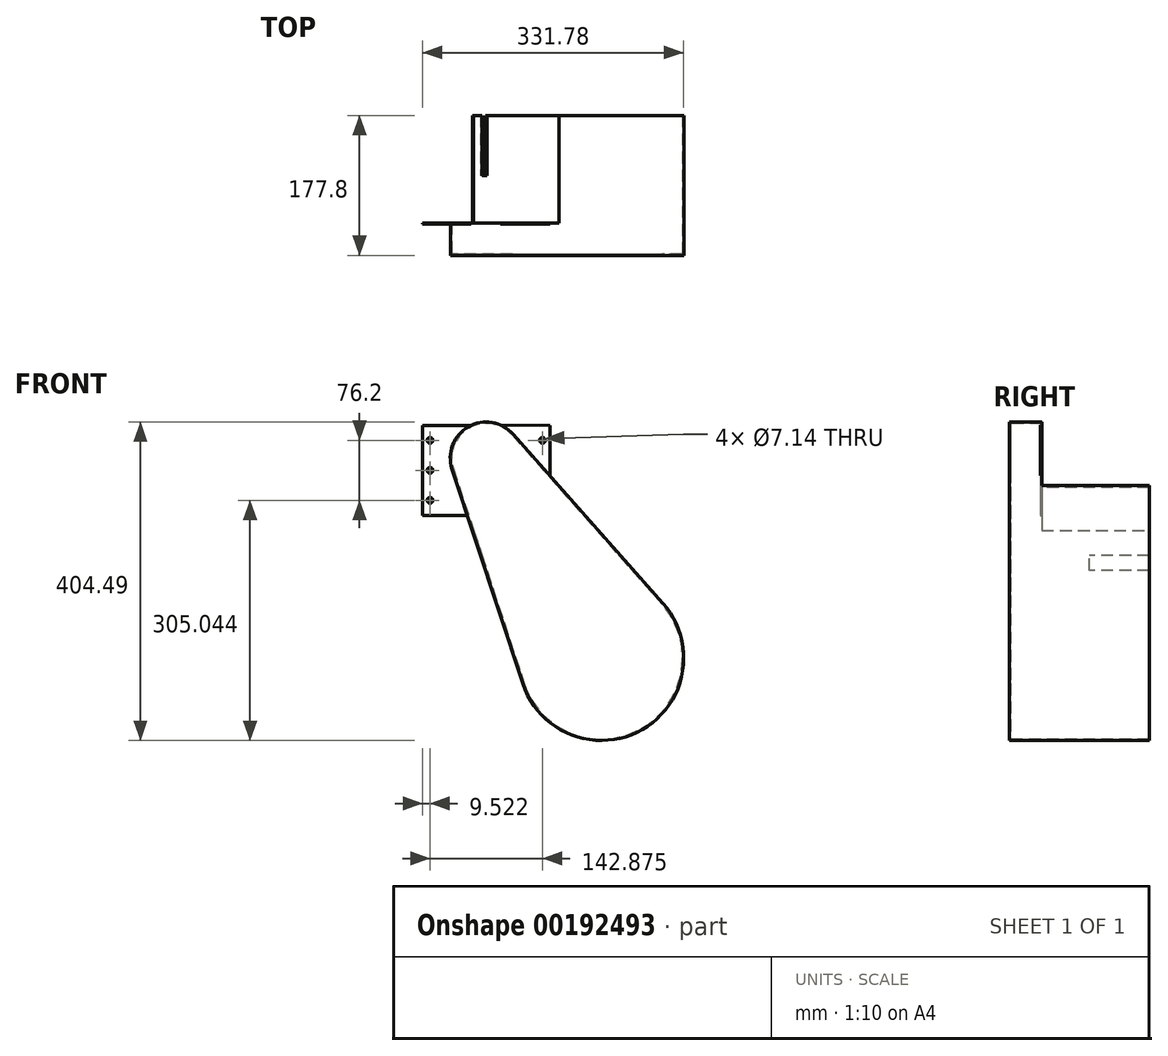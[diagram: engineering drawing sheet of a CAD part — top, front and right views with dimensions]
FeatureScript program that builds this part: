
annotation { "Feature Type Name" : "Feature", "Feature Type Description" : "" }
export const myFeature = defineFeature(function(context is Context, id is Id, definition is map)
    precondition{}
    {
        {
            var Q0;
            Q0=qCreatedBy(makeId("Front.planeOp"),FACE);
            var sketch = newSketch(context, id + "F0", { "sketchPlane" : qUnion([Q0])});
            skArc(sketch, "E0", {"start": v(34.23, 30.31) * mm, "mid": v(-22.8, 39.63) * mm, "end": v(-43.42, -14.33) * mm});
            skArc(sketch, "E1", {"start": v(46.56, -286.85) * mm, "mid": v(198.28, -344.83) * mm, "end": v(224.49, -184.54) * mm});
            skLineSegment(sketch, "E2", {"start": v(-43.42, -14.33) * mm, "end": v(46.56, -286.85) * mm});
            skLineSegment(sketch, "E3", {"start": v(34.23, 30.31) * mm, "end": v(224.49, -184.54) * mm});
            skSolve(sketch);
        }
        {
            var Q0;
            Q0 = qSketchRegion(id + "F0", true);
            extrude(context, id + "F1", {"entities" : qUnion([Q0]), "oppositeDirection" : true, "depth" : 177.8 * mm});
        }
        {
            var Q0;
            Q0=qCreatedBy(makeId("Right.planeOp"),FACE);
            cPlane(context, id + "F2", {"entities" : qUnion([Q0]), "cplaneType" : CPlaneType.OFFSET, "offset" : 92.07 * mm, "width" : 152.4 * mm, "height" : 152.4 * mm});
        }
        {
            var Q0;
            Q0=makeQuery(id+"F1.opExtrude","CAP_FACE",FACE,{"disambiguationData":[OSD([sQuery(id+"F0.wireOp",EDGE,"E0"),sQuery(id+"F0.wireOp",EDGE,"E1"),sQuery(id+"F0.wireOp",EDGE,"E2"),sQuery(id+"F0.wireOp",EDGE,"E3")])],"isStart":false});
            shell(context, id + "F3", {"entities" : qUnion([Q0]), "thickness" : 1.59 * mm});
        }
        {
            var Q0;
            Q0=qCreatedBy(id+"F2.planeOp",FACE);
            var sketch = newSketch(context, id + "F4", { "sketchPlane" : qUnion([Q0])});
            skLineSegment(sketch, "E4.bottom", {"start": v(242.86, -92.07) * mm, "end": v(41.28, -92.07) * mm});
            skLineSegment(sketch, "E4.top", {"start": v(242.86, 134.74) * mm, "end": v(41.27, 134.74) * mm});
            skLineSegment(sketch, "E4.left", {"start": v(242.86, -92.07) * mm, "end": v(242.86, 134.74) * mm});
            skLineSegment(sketch, "E4.right", {"start": v(41.28, -92.07) * mm, "end": v(41.27, 134.74) * mm});
            skSolve(sketch);
        }
        {
            var Q0;
            Q0 = qSketchRegion(id + "F4", true);
            extrude(context, id + "F5", {"entities" : qUnion([Q0]), "operationType" : NewBodyOperationType.REMOVE, "endBound" : BoundingType.THROUGH_ALL, "oppositeDirection" : true, "depth" : 25.4 * mm});
        }
        {
            var Q0;
            Q0=makeQuery(id+"F5.boolean.opBoolean","COPY",FACE,{"derivedFrom":makeQuery(id+"F5.opExtrude","SWEPT_FACE",FACE,{"disambiguationData":[OSD([sQuery(id+"F4.wireOp",EDGE,"E4.right")])]})});
            var sketch = newSketch(context, id + "F6", { "sketchPlane" : qUnion([Q0])});
            skCircle(sketch, "E5", {"center": v(71.44, 22.47) * mm, "radius": 3.57 * mm});
            skCircle(sketch, "E6.0.1.0", {"center": v(71.44, -15.63) * mm, "radius": 3.57 * mm});
            skCircle(sketch, "E6.0.2.0", {"center": v(71.44, -53.73) * mm, "radius": 3.57 * mm});
            skCircle(sketch, "E6.1.0.0", {"center": v(-71.44, 22.47) * mm, "radius": 3.57 * mm});
            skLineSegment(sketch, "E6.direction1", {"start": v(-71.44, 22.47) * mm, "end": v(71.44, 22.47) * mm, "construction": true});
            skLineSegment(sketch, "E6.direction2", {"start": v(71.44, 22.47) * mm, "end": v(71.44, -15.63) * mm, "construction": true});
            skLineSegment(sketch, "E7", {"start": v(-80.96, 41.28) * mm, "end": v(-80.96, -24.86) * mm});
            skLineSegment(sketch, "E8", {"start": v(80.96, 41.28) * mm, "end": v(80.96, -73.03) * mm});
            skLineSegment(sketch, "E9", {"start": v(80.96, -73.03) * mm, "end": v(22.37, -73.03) * mm});
            skLineSegment(sketch, "E10", {"start": v(80.96, 41.28) * mm, "end": v(15.62, 41.27) * mm});
            skLineSegment(sketch, "E11", {"start": v(-80.96, 41.28) * mm, "end": v(-13.52, 42) * mm});
            skLineSegment(sketch, "E12.0", {"start": v(-33.04, 29.26) * mm, "end": v(-80.96, -24.86) * mm});
            skArc(sketch, "E13.0", {"start": v(-33.04, 29.26) * mm, "mid": v(-24.14, 36.95) * mm, "end": v(-13.52, 42) * mm});
            skLineSegment(sketch, "E14.0", {"start": v(41.9, -13.84) * mm, "end": v(22.37, -73.02) * mm});
            skPoint(sketch, "E15.orphan", {"position": v(-92.07, -37.4) * mm});
            skArc(sketch, "E16.trimOffspring", {"start": v(15.62, 41.28) * mm, "mid": v(39.83, 19) * mm, "end": v(41.9, -13.84) * mm});
            skPoint(sketch, "E17.orphan", {"position": v(16.08, -92.07) * mm});
            skSolve(sketch);
        }
        {
            var Q0;
            Q0 = qSketchRegion(id + "F6", true);
            extrude(context, id + "F7", {"entities" : qUnion([Q0]), "operationType" : NewBodyOperationType.ADD, "oppositeDirection" : true, "depth" : 1.59 * mm});
        }
        {
            var Q0;
            Q0=qCreatedBy(makeId("Right.planeOp"),FACE);
            cPlane(context, id + "F8", {"entities" : qUnion([Q0]), "cplaneType" : CPlaneType.OFFSET, "offset" : 152.4 * mm, "oppositeDirection" : true, "width" : 152.4 * mm, "height" : 152.4 * mm});
        }
        {
            var Q0;
            Q0=qCreatedBy(id+"F8.planeOp",FACE);
            var sketch = newSketch(context, id + "F9", { "sketchPlane" : qUnion([Q0])});
            skLineSegment(sketch, "E18.0", {"start": v(177.8, -123.82) * mm, "end": v(177.8, -142.88) * mm});
            skLineSegment(sketch, "E19.bottom", {"start": v(177.8, -142.88) * mm, "end": v(101.6, -142.88) * mm});
            skLineSegment(sketch, "E19.top", {"start": v(177.8, -123.82) * mm, "end": v(101.6, -123.82) * mm});
            skLineSegment(sketch, "E19.right", {"start": v(101.6, -142.87) * mm, "end": v(101.6, -123.82) * mm});
            skPoint(sketch, "E20.orphan", {"position": v(177.8, -92.07) * mm});
            skPoint(sketch, "E21.orphan", {"position": v(177.8, -286.85) * mm});
            skSolve(sketch);
        }
        {
            var Q0;
            Q0 = qSketchRegion(id + "F9", true);
            var Q1;
            Q1=makeQuery(id+"F3.opShell","OFFSET_FACE",FACE,{"disambiguationData":[OSD([sQuery(id+"F0.wireOp",EDGE,"E2")])]});
            extrude(context, id + "F10", {"entities" : qUnion([Q0]), "operationType" : NewBodyOperationType.REMOVE, "endBound" : BoundingType.UP_TO_SURFACE, "endBoundEntityFace" : qUnion([Q1]), "depth" : 25.4 * mm});
        }
    });
